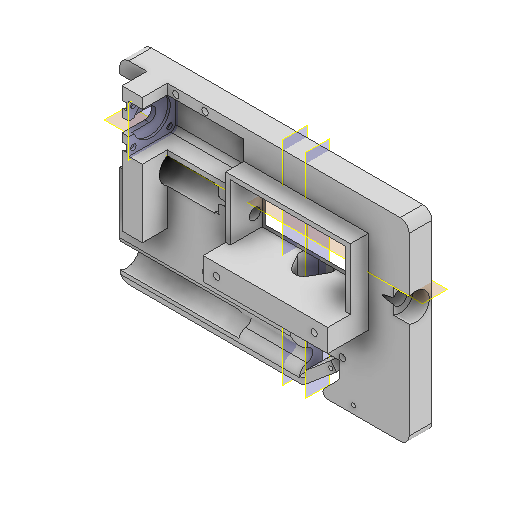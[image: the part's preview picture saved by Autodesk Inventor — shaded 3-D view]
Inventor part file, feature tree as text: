
AUTODESK INVENTOR PART (.ipt)
format: ipt  version: 2022 (Build 260153000, 153)  size: 684,544 bytes
history: native  units: mm
features: sketch x27, extrude x26, projected_geometry x14, reference x8, other x7, plane x5, fillet x4, chamfer x1, mirror x1, hole x1
ambient origin geometry x8: Origin, YZ Plane, XZ Plane, XY Plane, X Axis, Y Axis, Z Axis, Center Point
bodies: Solid1 (feature_tree)
feature tree (94):
  extrude  "Extrusion1"  Depth=85.5mm
  fillet  "Fillet1"  Radius=10.0mm
  extrude  "Extrusion2"  Depth=4.0mm
  extrude  "Extrusion3"  Depth=20.0mm
  plane  "Work Plane1"
  plane  "Work Plane2"
  chamfer  "Chamfer1"  [1 undecoded]
  extrude  "Extrusion4"  Depth=10.0mm
  extrude  "Extrusion5"  Depth=1.9mm
  extrude  "Extrusion6"  Depth=4.0mm TaperAngle=0.0deg
  extrude  "Extrusion7"  Depth=18.0mm TaperAngle=0.0deg
  extrude  "Extrusion8"  Depth=2.1mm
  plane  "Work Plane3"
  extrude  "Extrusion9"  Depth=6.0mm TaperAngle=0.0deg
  extrude  "Extrusion10"  Depth=10.0mm TaperAngle=0.0deg
  fillet  "Fillet3"  Radius=10.0mm
  extrude  "Extrusion11"  Depth=10.0mm
  extrude  "Extrusion12"  Depth=4.0mm
  extrude  "Extrusion13"  Depth=2.8mm
  mirror  "Mirror1"
  plane  "Work Plane4"
  extrude  "Extrusion14"  Depth=2.0mm
  sketch  "Sketch15"  dims[d39=20.0mm d40=10.0mm d41=0.0mm d42=0.0mm d44=12.2mm]
  plane  "Work Plane5"
  extrude  "Extrusion15"  Depth=2.0mm
  extrude  "Extrusion16"  Depth=12.0mm
  hole  "Hole1"  [1 undecoded]
  extrude  "Extrusion17"  Depth=2.8mm
  extrude  "Extrusion18"  Depth=12.0mm
  extrude  "Extrusion19"  Depth=0.5mm
  extrude  "Extrusion20"  Depth=4.0mm
  extrude  "Extrusion21"  Depth=10.0mm TaperAngle=0.0deg
  fillet  "Fillet4"  Radius=19.0mm
  extrude  "Extrusion22"  Depth=2.0mm
  extrude  "Extrusion23"  Depth=10.0mm TaperAngle=0.0deg
  extrude  "Extrusion24"  Depth=2.0mm
  fillet  "Fillet5"  Radius=12.9mm
  extrude  "Extrusion25"  Depth=2.0mm TaperAngle=0.0deg
  extrude  "Extrusion26"  Depth=2.0mm
  sketch  "Sketch1"  dims[d0=127.8mm d1=85.5mm d2=10.0mm d3=0.0mm]
  sketch  "Sketch2"  dims[d4=4.0mm d5=51.0mm]
  projected_geometry  "Projected Loop1"
  sketch  "Sketch3"  dims[d6=25.0mm d7=20.0mm]
  projected_geometry  "Projected Loop2"
  sketch  "Sketch4"  dims[d8=15.0mm]
  projected_geometry  "Projected Loop3"
  sketch  "Sketch5"  dims[d9=6.0mm]
  sketch  "Sketch6"  dims[d10=0.0mm]
  reference  "Reference2"
  sketch  "Sketch7"  dims[d11=1.5mm d12=0.0mm d13=0.0mm]
  sketch  "Sketch8"  dims[d14=4.0mm d15=2.0mm d16=45.0deg d17=10.0mm]
  reference  "Reference3"
  sketch  "Sketch9"  dims[d18=8.0mm d19=0.0mm d20=1.9mm]
  projected_geometry  "Projected Loop4"
  sketch  "Sketch10"  dims[d21=4.0mm d22=5.0mm d23=0.0mm]
  sketch  "Sketch11"  dims[d27=20.0mm d28=18.0mm d29=0.0mm]
  projected_geometry  "Projected Loop5"
  sketch  "Sketch12"  dims[d30=45.0deg d31=2.1mm]
  reference  "Reference4"
  sketch  "Sketch13"  dims[d32=7.0mm d33=6.0mm d34=0.0mm]
  sketch  "Sketch14"  dims[d35=6.0mm d36=8.0mm d37=0.0mm d38=10.0mm]
  reference  "Reference5"
  projected_geometry  "Projected Loop6"
  sketch  "Sketch16"  dims[d45=0.0mm d46=0.0mm d47=4.0mm]
  reference  "Reference6"
  sketch  "Sketch17"  dims[d48=2.8mm d49=2.8mm]
  reference  "Reference7"
  sketch  "Sketch18"  dims[d50=0.0mm d51=0.0mm d52=2.0mm]
  sketch  "Sketch19"  dims[d53=2.0mm d54=2.0mm]
  reference  "Reference10"
  sketch  "Sketch20"  dims[d55=32.0mm d56=12.0mm]
  sketch  "Sketch21"  dims[d57=2.8mm d58=2.8mm]
  projected_geometry  "Projected Loop7"
  sketch  "Sketch22"  dims[d59=2.8mm d60=2.8mm]
  projected_geometry  "Projected Loop8"
  sketch  "Sketch23"  dims[d61=30.0mm d62=-0.523599mm d63=12.0mm]
  projected_geometry  "Projected Loop9"
  reference  "Reference11"
  sketch  "Sketch24"  dims[d64=7.0mm d65=0.0mm d66=0.5mm]
  projected_geometry  "Projected Loop10"
  projected_geometry  "Projected Loop11"
  sketch  "Sketch25"  dims[d67=40.0mm d68=0.0mm d69=4.0mm]
  sketch  "Sketch26"  dims[d70=10.0mm d71=0.0mm d72=50.0mm d73=0.0mm]
  projected_geometry  "Projected Loop12"
  sketch  "Sketch27"  dims[d74=2.5mm d75=6.0mm d76=5.0mm d77=14.0mm d78=90.0deg d79=30.0mm d80=20.594885mm d81=19.0mm d82=16.0mm d83=10.0mm d84=0.0mm d85=9.0mm d86=12.9mm d87=30.0mm d88=0.0mm d89=30.0mm d90=30.0mm d91=0.0mm d92=2.0mm d93=0.0mm d94=1.0mm d95=0.0mm d96=2.8mm d97=2.8mm d98=2.8mm d99=2.8mm d100=7.0mm d101=10.0mm d102=0.0mm d103=11.8mm d104=2.0mm d105=2.8mm d106=2.8mm d107=6.0mm d108=6.0mm d109=0.0mm d110=0.0mm d113=8.0mm d114=0.0mm d115=0.0mm d116=0.0mm d117=17.5mm d118=17.5mm d119=5.922006mm d120=2.961003mm d121=8.726646mm d122=2.0mm d123=18.0mm d124=4.0mm d125=4.0mm d126=8.0mm d127=0.0mm d128=2.0mm d129=45.0deg d130=10.0mm d131=1.8mm d132=1.8mm d133=2.0mm d134=2.0mm d135=0.0mm d136=0.0mm d137=1.8mm d138=1.8mm d139=0.0mm d140=0.0mm]
  projected_geometry  "Projected Loop13"
  projected_geometry  "Projected Loop14"
  other  "<userpath>\Documents\GitHub\Guinardia\INVENTOR\Assembly_Guinardia_V0.iam"
  other  "Assembly_Guinardia_V0.iam"
  other  "00_CCTV_lens_M12_25mm_5mp:1"
  other  "00_PipetteTip200ul-1:2"
  other  "00_NEMA8:1"
  other  "00_PipetteTip200ul-1:3"
  other  "<userpath>\Documents\Inventor\Guinardia\INVENTOR\Assembly_Guinardia_V0.iam"
note: 2 required parameter values undecoded (feature->parameter linkage not recoverable at this tier; creation-order binding heuristic only, values carry confidence <= 0.55)
